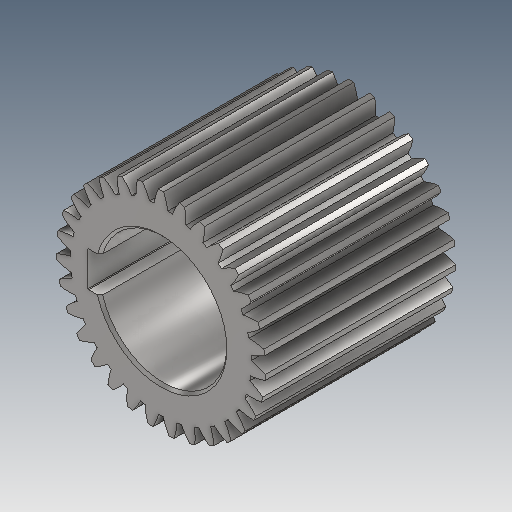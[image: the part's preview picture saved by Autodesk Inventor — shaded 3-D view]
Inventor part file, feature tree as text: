
AUTODESK INVENTOR PART (.ipt)
format: ipt  version: 2025 (Build 290162000, 162)  size: 430,592 bytes
history: native  units: mm (DEFAULTED — no unit token found)
features: other x5, plane x3, extrude x2, sketch x2, chamfer x1
ambient origin geometry x8: Origin, YZ Plane, XZ Plane, XY Plane, X Axis, Y Axis, Z Axis, Center Point
bodies: Solid1 (feature_tree)
feature tree (13):
  other  "{BB8FE430-83BF-418D-8DF9-9B323D3DB9B9}"
  extrude  "Extrusion1"  Depth=75.0mm TaperAngle=0.0deg
  plane  "Work Plane2"
  plane  "Work Plane8"
  plane  "Work Plane9"
  other  "正齿轮"
  extrude  "拉伸2"  Depth=10.0mm TaperAngle=0.0deg
  chamfer  "倒角1"  Distance=166.25mm
  other  "键槽3"
  sketch  "Sketch1"  dims[d0=82.5mm d1=75.0mm d2=0.0mm]
  other  "Srf1"
  sketch  "草图3"  dims[d3=77.5mm d4=10.0mm d5=0.0mm d16=166.25mm d17=0.0mm d34=1.013417mm d39=0.0mm d41=0.0mm d43=166.25mm d46=166.25mm d47=0.0mm d48=0.0mm d49=50.0mm d50=10.0mm d51=0.0mm d52=1.0mm d53=2.0mm d54=45.0deg d55=14.0mm d56=9.0mm]
  other  "轮毂键槽"
